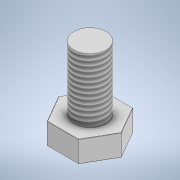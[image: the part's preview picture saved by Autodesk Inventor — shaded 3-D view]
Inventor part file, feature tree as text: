
AUTODESK INVENTOR PART (.ipt)
format: ipt  version: 2020 (Build 240168000, 168)  size: 128,512 bytes
history: native  units: mm
features: extrude x2, sketch x2, other x1, thread x1, fillet x1
ambient origin geometry x8: Origin, YZ Plane, XZ Plane, XY Plane, X Axis, Y Axis, Z Axis, Center Point
bodies: Body1 (feature_tree)
feature tree (7):
  other  "Твердое тело1"
  extrude  "Выдавливание1"  Depth=17.0mm
  extrude  "Выдавливание2"  Depth=6.69mm TaperAngle=0.0deg
  thread  "Резьба1"
  fillet  "Сопряжение1"  Radius=10.0mm
  sketch  "Эскиз1"
  sketch  "Эскиз2"
